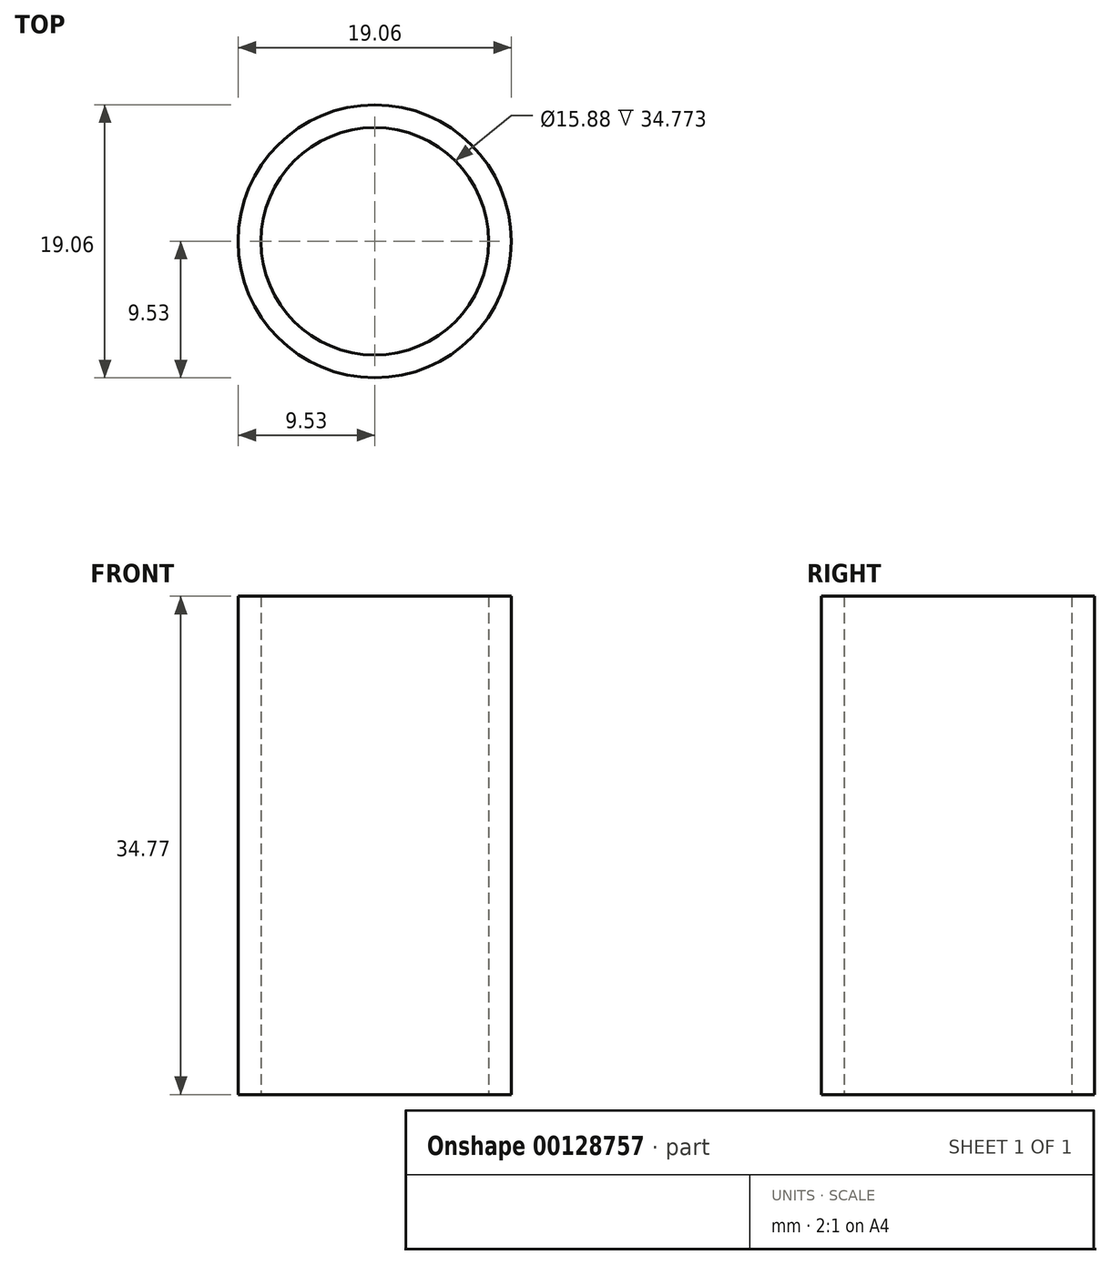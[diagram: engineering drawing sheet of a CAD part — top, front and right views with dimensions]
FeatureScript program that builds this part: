
annotation { "Feature Type Name" : "Feature", "Feature Type Description" : "" }
export const myFeature = defineFeature(function(context is Context, id is Id, definition is map)
    precondition{}
    {
        {
            var Q0;
            Q0=qCreatedBy(makeId("Top.planeOp"),FACE);
            var sketch = newSketch(context, id + "F0", { "sketchPlane" : qUnion([Q0])});
            skCircle(sketch, "E0", {"center": v(0, 0) * mm, "radius": 9.53 * mm});
            skCircle(sketch, "E1", {"center": v(0, 0) * mm, "radius": 7.94 * mm});
            skSolve(sketch);
        }
        {
            var Q0;
            Q0=makeQuery(id+"F0.imprint","IMPRINT",FACE,{"disambiguationData":[TD([[makeQuery(id+"F0.imprint","IMPRINT",EDGE,{"derivedFrom":sQuery(id+"F0.wireOp",EDGE,"E0")}),1.0]])]});
            extrude(context, id + "F1", {"entities" : qUnion([Q0]), "depth" : 34.77 * mm});
        }
    });
